# Revit family: Signage-NovaPolymers_Title-24-Unisex
name_source: partatom
category: Specialty Equipment
units: mm (PartAtom-declared; Revit-internal decimal feet)

## family parameters
Classification Number = 23.40.90.11.11
Cut with Voids When Loaded = No
Enable Cutting in Views = No
Host = Face
Maintain Annotation Orientation = No
Part Type = Normal
Room Calculation Point = No
Round Connector Dimension = Use Diameter
Shared = No

## types (1)
- Signage-NovaPolymers_Title-24-Unisex
    Assembly Code = C1030510
    Building Codes = http://www.novapolymers.com
    D635_Rate of Burning = Classification CC1 at nominal 0.060 inch (1.5 mm) thickness
    Default Elevation = 3' - 0"
    Description = Nova Polymers Signage as Specified in 10 14 36
    E84_Surface Burning Characteristics = Flame spread/smoke developed rating less than 75/120
    Expected Lifespan (Years) = 0
    Frame Overlap = 0' - 0 1/4"
    Frame Thickness = 0' - 0 1/8"
    Green Building-LEED = http://www.arcat.com
    Installation-Fabrication = http://www.novapolymers.com
    Keynote = 10 14 36
    Maintenance Schedule (Months) = 0
    Manufacturer = Nova Polymers, Inc.
    Manufacturer Fax = 973-882-0237
    Manufacturer Website = http://www.novapolymers.com
    Model = As Specified in 10 14 36
    Panel Attachment = Attachment : As Specified in Section 10 14 36
    Panel Thickness = 0' - 0 1/4"
    Product Data = http://www.arcat.com
    Product Properties = http://www.arcat.com
    Sales Information = http://www.novapolymers.com
    Send Message = http://admin.arcat.com
    SpecWizard = http://www.arcat.com
    Specification = http://www.arcat.com
    URL = http://www.novapolymers.com
    Vertical Burning = 94V-2 in thickness of 0.118 inch (3.0 mm) or greater and 94HB in thicknesses less than 0.118 inch (3.0 mm)
    Warranty Duration (Years) = 0

## geometry (parser evidence)
native form markers: Blend x98, Sweep x6
no freeform markers — native parametric forms only
